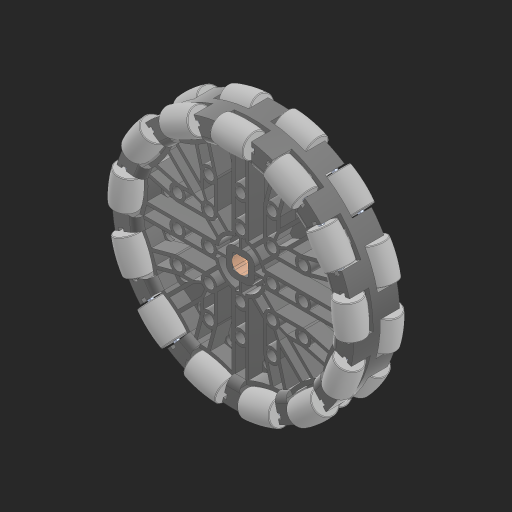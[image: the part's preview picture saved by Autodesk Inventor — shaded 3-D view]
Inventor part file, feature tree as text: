
AUTODESK INVENTOR PART (.ipt)
format: ipt  version: 2023 (Build 270158000, 158)  size: 4,710,400 bytes
history: native  units: in
note: dims shown in document units (in); Inventor stores cm internally (conversion verified against a paired STEP export)
features: other x55, move_body x1, sketch x1, extrude x1
ambient origin geometry x8: Origin, YZ Plane, XZ Plane, XY Plane, X Axis, Y Axis, Z Axis, Center Point
bodies: Solid1 (feature_tree), Solid2 (feature_tree), Solid3 (feature_tree), Solid4 (feature_tree), Solid5 (feature_tree), Solid6 (feature_tree), Solid7 (feature_tree), Solid8 (feature_tree), Solid9 (feature_tree), Solid10 (feature_tree), Solid11 (feature_tree), Solid12 (feature_tree), Solid13 (feature_tree), Solid14 (feature_tree), Solid15 (feature_tree), Solid16 (feature_tree), Solid17 (feature_tree), Solid18 (feature_tree), Solid19 (feature_tree), Solid20 (feature_tree), Solid21 (feature_tree), Solid22 (feature_tree), Solid23 (feature_tree), Solid24 (feature_tree), Solid25 (feature_tree), Solid26 (feature_tree), Solid27 (feature_tree), Solid28 (feature_tree), Solid29 (feature_tree), Solid30 (feature_tree), Solid31 (feature_tree), Solid32 (feature_tree), Solid33 (feature_tree), Solid34 (feature_tree), Solid35 (feature_tree), Solid36 (feature_tree), Solid37 (feature_tree), Solid38 (feature_tree), Solid39 (feature_tree), Solid40 (feature_tree), Solid41 (feature_tree), Solid42 (feature_tree), Solid43 (feature_tree), Solid44 (feature_tree), Solid45 (feature_tree), Solid46 (feature_tree), Solid47 (feature_tree), Solid48 (feature_tree), Solid49 (feature_tree), Solid50 (feature_tree), Solid51 (feature_tree), Solid52 (feature_tree), Solid53 (feature_tree)
feature tree (58):
  other  "4 (320mm Travel) Omni-Directional Anti-Static Wheel (276-8107).iam"
  other  "276-8107-001 Web.ipt:1"
  other  "276-8107-002 Web.iam:1::276-3526-001 Web.ipt:1"
  other  "276-8107-002 Web.iam:1::276-8107-003 Web.ipt:1"
  other  "276-8107-002 Web_1.iam:1::276-3526-001 Web.ipt:1"
  other  "276-8107-002 Web_1.iam:1::276-8107-003 Web.ipt:1"
  other  "276-8107-002 Web_2.iam:1::276-3526-001 Web.ipt:1"
  other  "276-8107-002 Web_2.iam:1::276-8107-003 Web.ipt:1"
  other  "276-8107-002 Web_3.iam:1::276-3526-001 Web.ipt:1"
  other  "276-8107-002 Web_3.iam:1::276-8107-003 Web.ipt:1"
  other  "276-8107-002 Web_4.iam:1::276-3526-001 Web.ipt:1"
  other  "276-8107-002 Web_4.iam:1::276-8107-003 Web.ipt:1"
  other  "276-8107-002 Web_5.iam:1::276-3526-001 Web.ipt:1"
  other  "276-8107-002 Web_5.iam:1::276-8107-003 Web.ipt:1"
  other  "276-8107-002 Web_6.iam:1::276-3526-001 Web.ipt:1"
  other  "276-8107-002 Web_6.iam:1::276-8107-003 Web.ipt:1"
  other  "276-8107-002 Web_7.iam:1::276-3526-001 Web.ipt:1"
  other  "276-8107-002 Web_7.iam:1::276-8107-003 Web.ipt:1"
  other  "276-8107-002 Web_8.iam:1::276-3526-001 Web.ipt:1"
  other  "276-8107-002 Web_8.iam:1::276-8107-003 Web.ipt:1"
  other  "276-8107-002 Web_9.iam:1::276-3526-001 Web.ipt:1"
  other  "276-8107-002 Web_9.iam:1::276-8107-003 Web.ipt:1"
  other  "276-8107-002 Web_10.iam:1::276-3526-001 Web.ipt:1"
  other  "276-8107-002 Web_10.iam:1::276-8107-003 Web.ipt:1"
  other  "276-8107-002 Web_11.iam:1::276-3526-001 Web.ipt:1"
  other  "276-8107-002 Web_11.iam:1::276-8107-003 Web.ipt:1"
  other  "276-8107-002 Web_12.iam:1::276-3526-001 Web.ipt:1"
  other  "276-8107-002 Web_12.iam:1::276-8107-003 Web.ipt:1"
  other  "276-8107-002 Web_13.iam:1::276-3526-001 Web.ipt:1"
  other  "276-8107-002 Web_13.iam:1::276-8107-003 Web.ipt:1"
  other  "276-8107-002 Web_14.iam:1::276-3526-001 Web.ipt:1"
  other  "276-8107-002 Web_14.iam:1::276-8107-003 Web.ipt:1"
  other  "276-8107-002 Web_15.iam:1::276-3526-001 Web.ipt:1"
  other  "276-8107-002 Web_15.iam:1::276-8107-003 Web.ipt:1"
  other  "276-8107-002 Web_16.iam:1::276-3526-001 Web.ipt:1"
  other  "276-8107-002 Web_16.iam:1::276-8107-003 Web.ipt:1"
  other  "276-8107-002 Web_17.iam:1::276-3526-001 Web.ipt:1"
  other  "276-8107-002 Web_17.iam:1::276-8107-003 Web.ipt:1"
  other  "276-8107-002 Web_18.iam:1::276-3526-001 Web.ipt:1"
  other  "276-8107-002 Web_18.iam:1::276-8107-003 Web.ipt:1"
  other  "276-8107-002 Web_19.iam:1::276-3526-001 Web.ipt:1"
  other  "276-8107-002 Web_19.iam:1::276-8107-003 Web.ipt:1"
  other  "276-8107-002 Web_20.iam:1::276-3526-001 Web.ipt:1"
  other  "276-8107-002 Web_20.iam:1::276-8107-003 Web.ipt:1"
  other  "276-8107-002 Web_21.iam:1::276-3526-001 Web.ipt:1"
  other  "276-8107-002 Web_21.iam:1::276-8107-003 Web.ipt:1"
  other  "276-8107-002 Web_22.iam:1::276-3526-001 Web.ipt:1"
  other  "276-8107-002 Web_22.iam:1::276-8107-003 Web.ipt:1"
  other  "276-8107-002 Web_23.iam:1::276-3526-001 Web.ipt:1"
  other  "276-8107-002 Web_23.iam:1::276-8107-003 Web.ipt:1"
  other  "276-8107-002 Web_24.iam:1::276-3526-001 Web.ipt:1"
  other  "276-8107-002 Web_24.iam:1::276-8107-003 Web.ipt:1"
  other  "276-8107-002 Web_25.iam:1::276-3526-001 Web.ipt:1"
  other  "276-8107-002 Web_25.iam:1::276-8107-003 Web.ipt:1"
  move_body  "Move Body1"
  sketch  "Sketch1"  dims[d0=0.3937in d1=90.0deg d2=0.25in d3=1.0in d4=0.0in]
  other  "Srf1"
  extrude  "ExtrusionSrf1"  TaperAngle=90.0deg  [1 undecoded]
note: 1 required parameter value undecoded (feature->parameter linkage not recoverable at this tier; creation-order binding heuristic only, values carry confidence <= 0.55)
